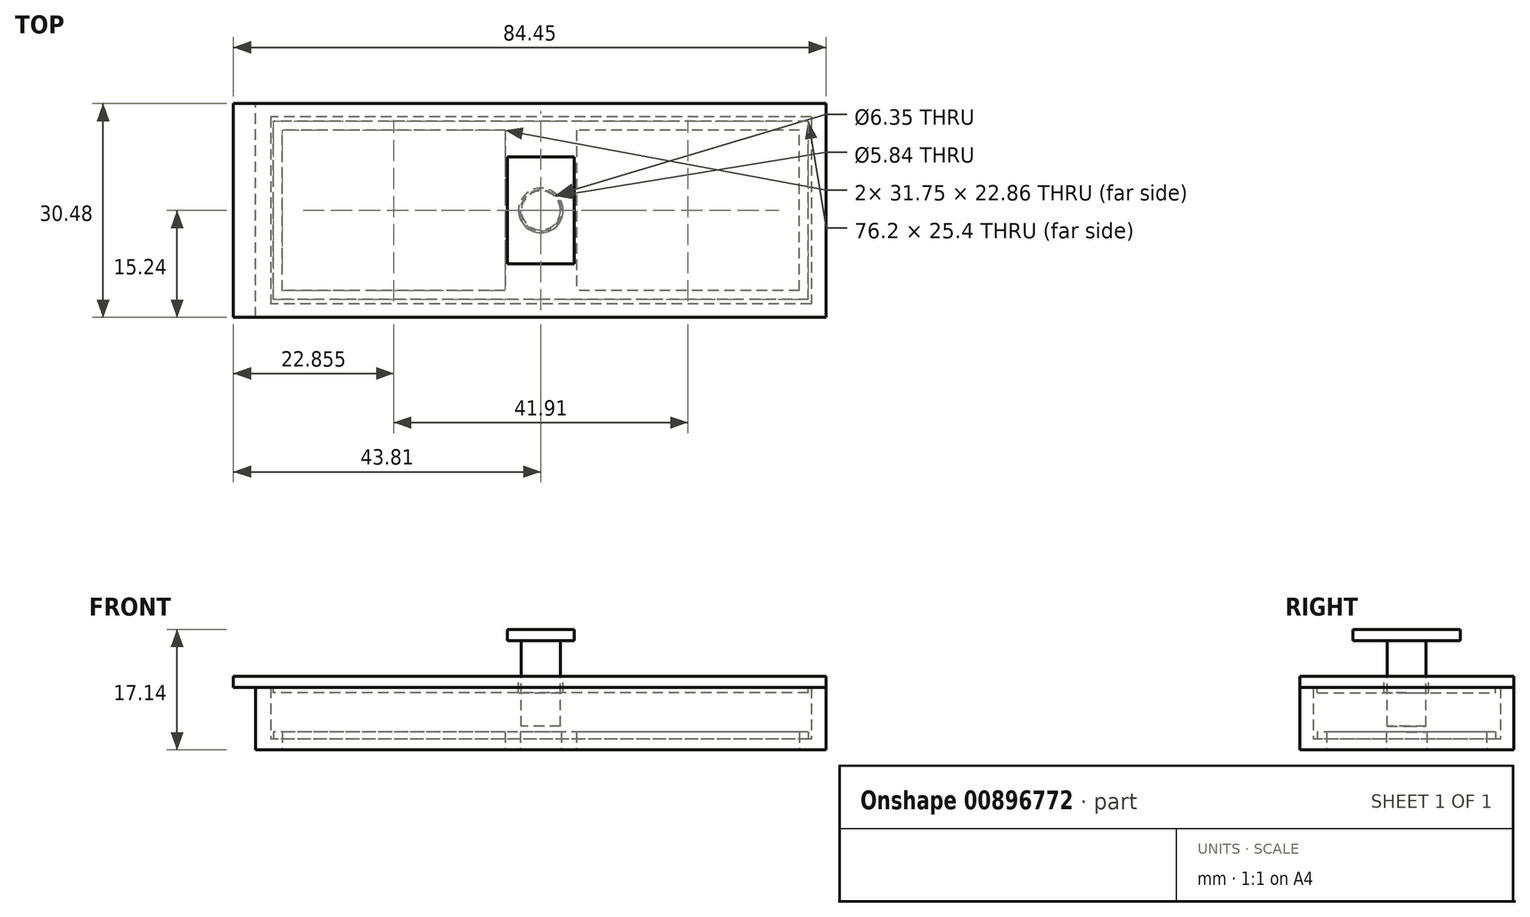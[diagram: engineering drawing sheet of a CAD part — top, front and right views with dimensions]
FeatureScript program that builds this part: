
annotation { "Feature Type Name" : "Feature", "Feature Type Description" : "" }
export const myFeature = defineFeature(function(context is Context, id is Id, definition is map)
    precondition{}
    {
        {
            var Q0;
            Q0=qCreatedBy(makeId("Top.planeOp"),FACE);
            var sketch = newSketch(context, id + "F0", { "sketchPlane" : qUnion([Q0])});
            skLineSegment(sketch, "E0.bottom", {"start": v(38.1, 12.7) * mm, "end": v(-38.1, 12.7) * mm});
            skLineSegment(sketch, "E0.top", {"start": v(38.1, -12.7) * mm, "end": v(-38.1, -12.7) * mm});
            skLineSegment(sketch, "E0.left", {"start": v(38.1, 12.7) * mm, "end": v(38.1, -12.7) * mm});
            skLineSegment(sketch, "E0.right", {"start": v(-38.1, 12.7) * mm, "end": v(-38.1, -12.7) * mm});
            skPoint(sketch, "E0.middle", {"position": v(0, 0) * mm});
            skSolve(sketch);
        }
        {
            var Q0;
            Q0 = qSketchRegion(id + "F0", true);
            extrude(context, id + "F1", {"entities" : qUnion([Q0]), "depth" : 1.02 * mm, "offsetDistance" : 25.4 * mm});
        }
        {
            var Q0;
            Q0=makeQuery(id+"F1.opExtrude","CAP_FACE",FACE,{"disambiguationData":[OSD([sQuery(id+"F0.wireOp",EDGE,"E0.bottom"),sQuery(id+"F0.wireOp",EDGE,"E0.top"),sQuery(id+"F0.wireOp",EDGE,"E0.left"),sQuery(id+"F0.wireOp",EDGE,"E0.right")])],"isStart":false});
            var sketch = newSketch(context, id + "F2", { "sketchPlane" : qUnion([Q0])});
            skLineSegment(sketch, "E1.bottom", {"start": v(40.64, -15.24) * mm, "end": v(-40.64, -15.24) * mm});
            skLineSegment(sketch, "E1.top", {"start": v(40.64, 15.24) * mm, "end": v(-40.64, 15.24) * mm});
            skLineSegment(sketch, "E1.left", {"start": v(40.64, 15.24) * mm, "end": v(40.64, -15.24) * mm});
            skLineSegment(sketch, "E1.right", {"start": v(-40.64, -15.24) * mm, "end": v(-40.64, 15.24) * mm});
            skPoint(sketch, "E1.middle", {"position": v(0, 0) * mm});
            skLineSegment(sketch, "E2.bottom", {"start": v(38.52, 13.34) * mm, "end": v(-38.52, 13.34) * mm});
            skLineSegment(sketch, "E2.top", {"start": v(38.52, -13.34) * mm, "end": v(-38.52, -13.34) * mm});
            skLineSegment(sketch, "E2.left", {"start": v(38.52, 13.34) * mm, "end": v(38.52, -13.34) * mm});
            skLineSegment(sketch, "E2.right", {"start": v(-38.52, 13.34) * mm, "end": v(-38.52, -13.34) * mm});
            skSolve(sketch);
        }
        {
            var Q0;
            Q0=makeQuery(id+"F2.imprint","IMPRINT",FACE,{"disambiguationData":[TD([[makeQuery(id+"F2.imprint","IMPRINT",EDGE,{"derivedFrom":sQuery(id+"F2.wireOp",EDGE,"E1.bottom")}),-1.0]])]});
            extrude(context, id + "F3", {"entities" : qUnion([Q0]), "depth" : 6.35 * mm, "offsetDistance" : 25.4 * mm, "hasSecondDirection" : true, "secondDirectionOppositeDirection" : true, "secondDirectionDepth" : 2.54 * mm});
        }
        {
            var Q0;
            Q0=makeQuery(id+"F3.opExtrude","CAP_FACE",FACE,{"disambiguationData":[OSD([sQuery(id+"F0.wireOp",EDGE,"E0.bottom"),sQuery(id+"F0.wireOp",EDGE,"E0.top"),sQuery(id+"F0.wireOp",EDGE,"E0.left"),sQuery(id+"F0.wireOp",EDGE,"E0.right"),sQuery(id+"F2.wireOp",EDGE,"E1.bottom"),sQuery(id+"F2.wireOp",EDGE,"E1.top"),sQuery(id+"F2.wireOp",EDGE,"E1.left"),sQuery(id+"F2.wireOp",EDGE,"E1.right")])],"isStart":true});
            var sketch = newSketch(context, id + "F4", { "sketchPlane" : qUnion([Q0])});
            skLineSegment(sketch, "E3.bottom", {"start": v(38.52, 13.34) * mm, "end": v(-38.52, 13.34) * mm});
            skLineSegment(sketch, "E3.top", {"start": v(38.52, -13.34) * mm, "end": v(-38.52, -13.34) * mm});
            skLineSegment(sketch, "E3.left", {"start": v(38.52, 13.34) * mm, "end": v(38.52, -13.34) * mm});
            skLineSegment(sketch, "E3.right", {"start": v(-38.52, 13.34) * mm, "end": v(-38.52, -13.34) * mm});
            skPoint(sketch, "E3.middle", {"position": v(0, 0) * mm});
            skSolve(sketch);
        }
        {
            var Q0;
            Q0 = qSketchRegion(id + "F4", true);
            var Q1;
            Q1=makeQuery(id+"F1.opExtrude","CAP_FACE",FACE,{"disambiguationData":[OSD([sQuery(id+"F0.wireOp",EDGE,"E0.bottom"),sQuery(id+"F0.wireOp",EDGE,"E0.top"),sQuery(id+"F0.wireOp",EDGE,"E0.left"),sQuery(id+"F0.wireOp",EDGE,"E0.right")])],"isStart":true});
            extrude(context, id + "F5", {"entities" : qUnion([Q0]), "operationType" : NewBodyOperationType.ADD, "endBound" : BoundingType.UP_TO_SURFACE, "oppositeDirection" : true, "depth" : 25.4 * mm, "endBoundEntityFace" : qUnion([Q1]), "offsetDistance" : 25.4 * mm});
        }
        {
            var Q0;
            Q0=makeQuery(id+"F3.opExtrude","CAP_FACE",FACE,{"disambiguationData":[OSD([sQuery(id+"F2.wireOp",EDGE,"E1.bottom"),sQuery(id+"F2.wireOp",EDGE,"E1.top"),sQuery(id+"F2.wireOp",EDGE,"E1.left"),sQuery(id+"F2.wireOp",EDGE,"E1.right"),sQuery(id+"F2.wireOp",EDGE,"E2.bottom"),sQuery(id+"F2.wireOp",EDGE,"E2.top"),sQuery(id+"F2.wireOp",EDGE,"E2.left"),sQuery(id+"F2.wireOp",EDGE,"E2.right")])],"isStart":false});
            var sketch = newSketch(context, id + "F6", { "sketchPlane" : qUnion([Q0])});
            skLineSegment(sketch, "E4.bottom", {"start": v(-43.81, 15.24) * mm, "end": v(40.64, 15.24) * mm});
            skLineSegment(sketch, "E4.top", {"start": v(-43.81, -15.24) * mm, "end": v(40.64, -15.24) * mm});
            skLineSegment(sketch, "E4.left", {"start": v(-43.81, 15.24) * mm, "end": v(-43.81, -15.24) * mm});
            skLineSegment(sketch, "E4.right", {"start": v(40.64, 15.24) * mm, "end": v(40.64, -15.24) * mm});
            skSolve(sketch);
        }
        {
            var Q0;
            Q0 = qSketchRegion(id + "F6", true);
            extrude(context, id + "F7", {"entities" : qUnion([Q0]), "depth" : 1.59 * mm, "offsetDistance" : 25.4 * mm});
        }
        {
            var Q0;
            Q0=makeQuery(id+"F7.opExtrude","CAP_FACE",FACE,{"disambiguationData":[OSD([sQuery(id+"F6.wireOp",EDGE,"E4.bottom"),sQuery(id+"F6.wireOp",EDGE,"E4.top"),sQuery(id+"F6.wireOp",EDGE,"E4.left"),sQuery(id+"F6.wireOp",EDGE,"E4.right")])],"isStart":true});
            var sketch = newSketch(context, id + "F8", { "sketchPlane" : qUnion([Q0])});
            skLineSegment(sketch, "E5.bottom", {"start": v(38.1, 12.7) * mm, "end": v(-38.1, 12.7) * mm});
            skLineSegment(sketch, "E5.top", {"start": v(38.1, -12.7) * mm, "end": v(-38.1, -12.7) * mm});
            skLineSegment(sketch, "E5.left", {"start": v(38.1, 12.7) * mm, "end": v(38.1, -12.7) * mm});
            skLineSegment(sketch, "E5.right", {"start": v(-38.1, 12.7) * mm, "end": v(-38.1, -12.7) * mm});
            skPoint(sketch, "E5.middle", {"position": v(0, 0) * mm});
            skSolve(sketch);
        }
        {
            var Q0;
            Q0 = qSketchRegion(id + "F8", true);
            extrude(context, id + "F9", {"entities" : qUnion([Q0]), "operationType" : NewBodyOperationType.ADD, "depth" : 0.8 * mm, "offsetDistance" : 25.4 * mm});
        }
        {
            var Q0;
            Q0=makeQuery(id+"F7.opExtrude","CAP_FACE",FACE,{"disambiguationData":[OSD([sQuery(id+"F6.wireOp",EDGE,"E4.bottom"),sQuery(id+"F6.wireOp",EDGE,"E4.top"),sQuery(id+"F6.wireOp",EDGE,"E4.left"),sQuery(id+"F6.wireOp",EDGE,"E4.right")])],"isStart":false});
            var sketch = newSketch(context, id + "F10", { "sketchPlane" : qUnion([Q0])});
            skCircle(sketch, "E6", {"center": v(0, 0) * mm, "radius": 3.17 * mm});
            skSolve(sketch);
        }
        {
            var Q0;
            Q0 = qSketchRegion(id + "F10", true);
            extrude(context, id + "F11", {"entities" : qUnion([Q0]), "operationType" : NewBodyOperationType.REMOVE, "endBound" : BoundingType.UP_TO_NEXT, "oppositeDirection" : true, "depth" : 25.4 * mm, "offsetDistance" : 25.4 * mm});
        }
        {
            var Q0;
            Q0=makeQuery(id+"F7.opExtrude","CAP_FACE",FACE,{"disambiguationData":[OSD([sQuery(id+"F6.wireOp",EDGE,"E4.bottom"),sQuery(id+"F6.wireOp",EDGE,"E4.top"),sQuery(id+"F6.wireOp",EDGE,"E4.left"),sQuery(id+"F6.wireOp",EDGE,"E4.right")])],"isStart":false});
            var sketch = newSketch(context, id + "F12", { "sketchPlane" : qUnion([Q0])});
            skCircle(sketch, "E7", {"center": v(0, 0) * mm, "radius": 2.78 * mm});
            skSolve(sketch);
        }
        {
            var Q0;
            Q0 = qSketchRegion(id + "F12", true);
            extrude(context, id + "F13", {"entities" : qUnion([Q0]), "oppositeDirection" : true, "depth" : 7.14 * mm, "offsetDistance" : 25.4 * mm, "hasSecondDirection" : true, "secondDirectionOppositeDirection" : false, "secondDirectionDepth" : 5.08 * mm});
        }
        {
            var Q0;
            Q0=makeQuery(id+"F13.opExtrude","CAP_FACE",FACE,{"disambiguationData":[OSD([sQuery(id+"F12.wireOp",EDGE,"E7")])],"isStart":true});
            var sketch = newSketch(context, id + "F14", { "sketchPlane" : qUnion([Q0])});
            skLineSegment(sketch, "E8.bottom", {"start": v(4.76, 7.62) * mm, "end": v(-4.76, 7.62) * mm});
            skLineSegment(sketch, "E8.top", {"start": v(4.76, -7.62) * mm, "end": v(-4.76, -7.62) * mm});
            skLineSegment(sketch, "E8.left", {"start": v(4.76, 7.62) * mm, "end": v(4.76, -7.62) * mm});
            skLineSegment(sketch, "E8.right", {"start": v(-4.76, 7.62) * mm, "end": v(-4.76, -7.62) * mm});
            skPoint(sketch, "E8.middle", {"position": v(0, 0) * mm});
            skSolve(sketch);
        }
        {
            var Q0;
            Q0 = qSketchRegion(id + "F14", true);
            extrude(context, id + "F15", {"entities" : qUnion([Q0]), "operationType" : NewBodyOperationType.ADD, "depth" : 1.59 * mm, "offsetDistance" : 25.4 * mm});
        }
        {
            var Q0;
            Q0=makeQuery(id+"F5.boolean.opBoolean","MERGE",FACE,{"derivedFrom":[makeQuery(id+"F3.opExtrude","CAP_FACE",FACE,{"disambiguationData":[OSD([sQuery(id+"F2.wireOp",EDGE,"E1.bottom"),sQuery(id+"F2.wireOp",EDGE,"E1.top"),sQuery(id+"F2.wireOp",EDGE,"E1.left"),sQuery(id+"F2.wireOp",EDGE,"E1.right"),sQuery(id+"F2.wireOp",EDGE,"E2.bottom"),sQuery(id+"F2.wireOp",EDGE,"E2.top"),sQuery(id+"F2.wireOp",EDGE,"E2.left"),sQuery(id+"F2.wireOp",EDGE,"E2.right")])],"isStart":true}),makeQuery(id+"F5.opExtrude","CAP_FACE",FACE,{"disambiguationData":[OSD([sQuery(id+"F4.wireOp",EDGE,"E3.bottom"),sQuery(id+"F4.wireOp",EDGE,"E3.top"),sQuery(id+"F4.wireOp",EDGE,"E3.left"),sQuery(id+"F4.wireOp",EDGE,"E3.right")])],"isStart":true})]});
            var sketch = newSketch(context, id + "F16", { "sketchPlane" : qUnion([Q0])});
            skLineSegment(sketch, "E9.bottom", {"start": v(36.83, 11.43) * mm, "end": v(-36.83, 11.43) * mm});
            skLineSegment(sketch, "E9.top", {"start": v(36.83, -11.43) * mm, "end": v(-36.83, -11.43) * mm});
            skLineSegment(sketch, "E9.left", {"start": v(36.83, 11.43) * mm, "end": v(36.83, -11.43) * mm});
            skLineSegment(sketch, "E9.right", {"start": v(-36.83, 11.43) * mm, "end": v(-36.83, -11.43) * mm});
            skPoint(sketch, "E9.middle", {"position": v(0, 0) * mm});
            skCircle(sketch, "E10", {"center": v(0, 0) * mm, "radius": 2.92 * mm});
            skLineSegment(sketch, "E11.bottom", {"start": v(5.08, -11.43) * mm, "end": v(-5.08, -11.43) * mm});
            skLineSegment(sketch, "E11.top", {"start": v(5.08, 11.43) * mm, "end": v(-5.08, 11.43) * mm});
            skLineSegment(sketch, "E11.left", {"start": v(5.08, -11.43) * mm, "end": v(5.08, 11.43) * mm});
            skLineSegment(sketch, "E11.right", {"start": v(-5.08, -11.43) * mm, "end": v(-5.08, 11.43) * mm});
            skSolve(sketch);
        }
        {
            var Q0;
            {var subQ0=sQuery(id+"F16.wireOp",EDGE,"E9.left");Q0=makeQuery(id+"F16.imprint","IMPRINT",FACE,{"disambiguationData":[TD([[makeQuery(id+"F16.imprint","IMPRINT",EDGE,{"derivedFrom":subQ0}),-1.0]])]});}
            var Q1;
            {var subQ0=sQuery(id+"F16.wireOp",EDGE,"E9.right");Q1=makeQuery(id+"F16.imprint","IMPRINT",FACE,{"disambiguationData":[TD([[makeQuery(id+"F16.imprint","IMPRINT",EDGE,{"derivedFrom":subQ0}),1.0]])]});}
            var Q2;
            Q2=makeQuery(id+"F16.imprint","IMPRINT",FACE,{"disambiguationData":[TD([[makeQuery(id+"F16.imprint","IMPRINT",EDGE,{"derivedFrom":sQuery(id+"F16.wireOp",EDGE,"E10")}),1.0]])]});
            extrude(context, id + "F17", {"entities" : qUnion([Q0, Q1, Q2]), "operationType" : NewBodyOperationType.REMOVE, "endBound" : BoundingType.UP_TO_NEXT, "oppositeDirection" : true, "depth" : 25.4 * mm, "offsetDistance" : 25.4 * mm});
        }
    });
